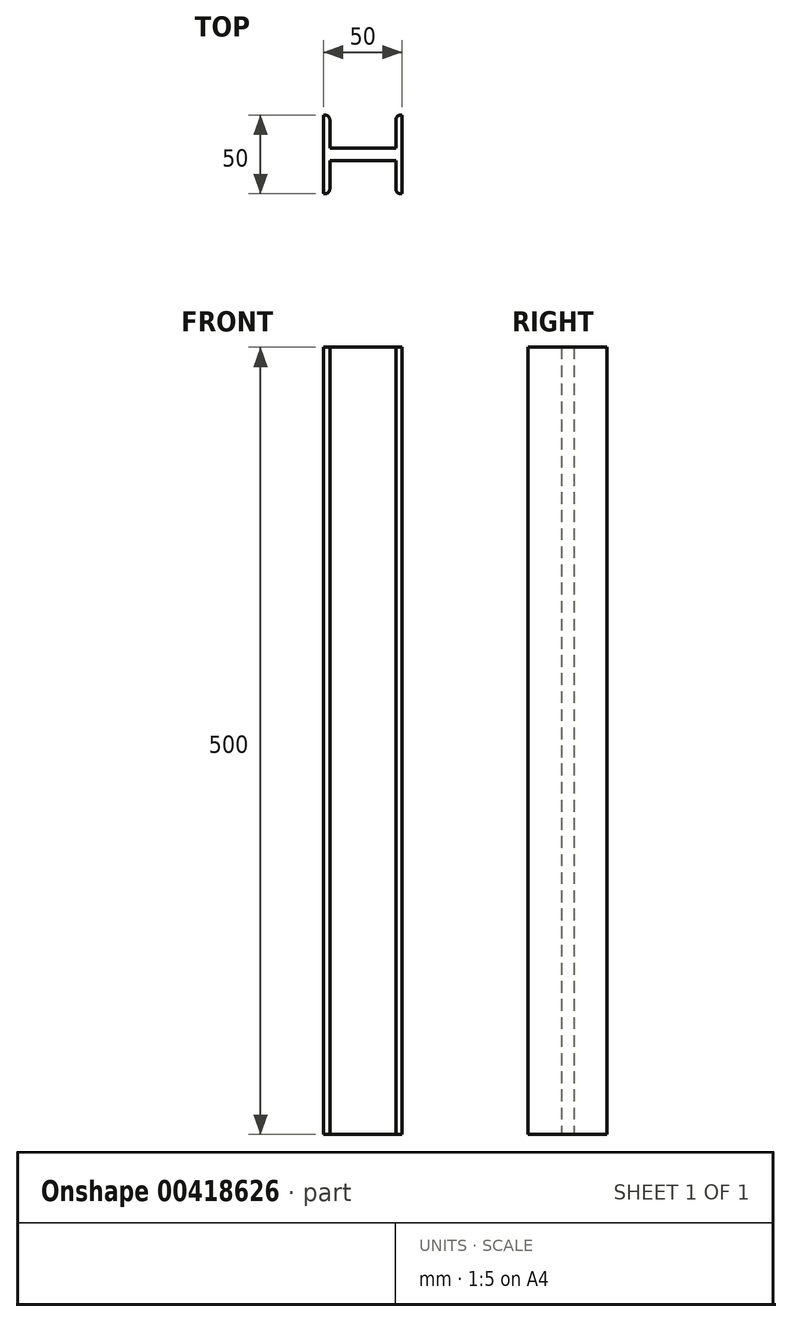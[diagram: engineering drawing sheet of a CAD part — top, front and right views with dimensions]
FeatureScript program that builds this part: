
annotation { "Feature Type Name" : "Feature", "Feature Type Description" : "" }
export const myFeature = defineFeature(function(context is Context, id is Id, definition is map)
    precondition{}
    {
        {
            var Q0;
            Q0=qCreatedBy(makeId("Front.planeOp"),FACE);
            var sketch = newSketch(context, id + "F0", { "sketchPlane" : qUnion([Q0])});
            skLineSegment(sketch, "E0.bottom", {"start": v(-10.24, 24.65) * mm, "end": v(39.76, 24.65) * mm});
            skLineSegment(sketch, "E0.top", {"start": v(-10.24, -475.35) * mm, "end": v(39.76, -475.35) * mm});
            skLineSegment(sketch, "E0.left", {"start": v(-10.24, 24.65) * mm, "end": v(-10.24, -475.35) * mm});
            skLineSegment(sketch, "E0.right", {"start": v(39.76, 24.65) * mm, "end": v(39.76, -475.35) * mm});
            skLineSegment(sketch, "E1", {"start": v(-6.24, 24.65) * mm, "end": v(-6.24, -475.35) * mm});
            skLineSegment(sketch, "E2", {"start": v(35.76, 24.65) * mm, "end": v(35.76, -475.35) * mm});
            skSolve(sketch);
        }
        {
            var Q0;
            {var subQ0=sQuery(id+"F0.wireOp",EDGE,"E0.left");Q0=makeQuery(id+"F0.imprint","IMPRINT",FACE,{"disambiguationData":[TD([[makeQuery(id+"F0.imprint","IMPRINT",EDGE,{"derivedFrom":subQ0}),1.0]])]});}
            extrude(context, id + "F1", {"entities" : qUnion([Q0]), "depth" : 25 * mm});
        }
        {
            var Q0;
            {var subQ0=sQuery(id+"F0.wireOp",EDGE,"E1");Q0=makeQuery(id+"F0.imprint","IMPRINT",FACE,{"disambiguationData":[TD([[makeQuery(id+"F0.imprint","IMPRINT",EDGE,{"derivedFrom":subQ0}),1.0]])]});}
            extrude(context, id + "F2", {"entities" : qUnion([Q0]), "operationType" : NewBodyOperationType.ADD, "depth" : 4 * mm});
        }
        {
            var Q0;
            {var subQ0=sQuery(id+"F0.wireOp",EDGE,"E0.right");Q0=makeQuery(id+"F0.imprint","IMPRINT",FACE,{"disambiguationData":[TD([[makeQuery(id+"F0.imprint","IMPRINT",EDGE,{"derivedFrom":subQ0}),-1.0]])]});}
            extrude(context, id + "F3", {"entities" : qUnion([Q0]), "operationType" : NewBodyOperationType.ADD, "depth" : 25 * mm});
        }
        {
            var Q0;
            Q0=makeQuery(id+"F1.opExtrude","CAP_EDGE",EDGE,{"disambiguationData":[OSD([sQuery(id+"F0.wireOp",EDGE,"E1")])],"isStart":false});
            var Q1;
            Q1=makeQuery(id+"F3.opExtrude","CAP_EDGE",EDGE,{"disambiguationData":[OSD([sQuery(id+"F0.wireOp",EDGE,"E2")])],"isStart":false});
            var Q2;
            Q2=makeQuery(id+"F2.opExtrude","CAP_EDGE",EDGE,{"disambiguationData":[OSD([sQuery(id+"F0.wireOp",EDGE,"E1")])],"isStart":false});
            var Q3;
            Q3=makeQuery(id+"F2.opExtrude","CAP_EDGE",EDGE,{"disambiguationData":[OSD([sQuery(id+"F0.wireOp",EDGE,"E2")])],"isStart":false});
            fillet(context, id + "F4", {"entities" : qUnion([Q0, Q1, Q2, Q3]), "radius" : 3 * mm, "tangentPropagation" : true, "allowEdgeOverflow" : false});
        }
        {
            var Q0;
            Q0=makeQuery(id+"F1.opExtrude","SWEPT_BODY",BODY,{"disambiguationData":[OSD([sQuery(id+"F0.wireOp",EDGE,"E0.bottom"),sQuery(id+"F0.wireOp",EDGE,"E0.top"),sQuery(id+"F0.wireOp",EDGE,"E0.left"),sQuery(id+"F0.wireOp",EDGE,"E1")])]});
            var Q1;
            Q1=qCreatedBy(makeId("Front.planeOp"),FACE);
            mirror(context, id + "F5", {"operationType" : NewBodyOperationType.ADD, "entities" : qUnion([Q0]), "mirrorPlane" : qUnion([Q1])});
        }
    });
